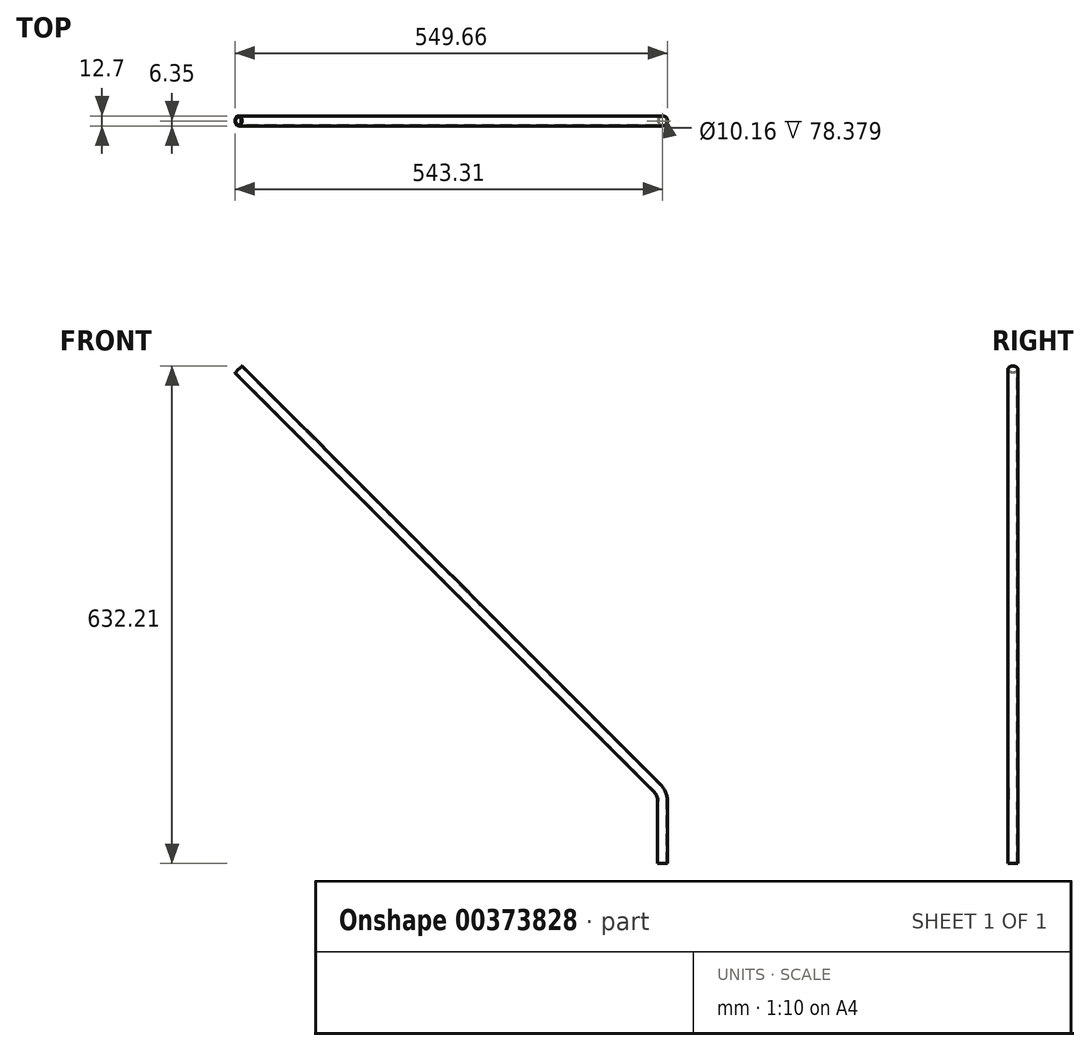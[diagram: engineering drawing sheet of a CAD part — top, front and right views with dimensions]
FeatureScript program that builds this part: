
annotation { "Feature Type Name" : "Feature", "Feature Type Description" : "" }
export const myFeature = defineFeature(function(context is Context, id is Id, definition is map)
    precondition{}
    {
        {
            var Q0;
            Q0=qCreatedBy(makeId("Top.planeOp"), FACE);
            var sketch = newSketch(context, id + "F0", { "sketchPlane" : qUnion([Q0])});
            skCircle(sketch, "E0", {"center": v(0, 0) * mm, "radius": 5.08 * mm});
            skCircle(sketch, "E1", {"center": v(0, 0) * mm, "radius": 6.35 * mm});
            skSolve(sketch);
        }
        {
            var Q0;
            Q0=qCreatedBy(makeId("Front.planeOp"), FACE);
            var sketch = newSketch(context, id + "F1", { "sketchPlane" : qUnion([Q0])});
            skLineSegment(sketch, "E2", {"start": v(0, 0) * mm, "end": v(0, 78.38) * mm});
            skLineSegment(sketch, "E3", {"start": v(-7.44, 96.34) * mm, "end": v(-538.82, 627.72) * mm});
            skPoint(sketch, "E4.visualSharp", {"position": v(0, 88.9) * mm});
            skArc(sketch, "E4.filletArc", {"start": v(0, 78.38) * mm, "mid": v(-1.93, 88.1) * mm, "end": v(-7.44, 96.34) * mm});
            skSolve(sketch);
        }
        {
            var Q0;
            Q0 = qSketchRegion(id + "F0", true);
            var Q1;
            Q1 = qConstructionFilter(qBodyType(qCreatedBy(id + "F1" ,EDGE), BodyType.WIRE), ConstructionObject.NO);
            sweep(context, id + "F2", {"profiles" : qUnion([Q0]), "path" : qUnion([Q1])});
        }
    });
